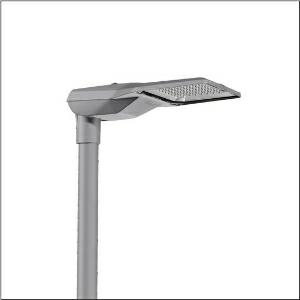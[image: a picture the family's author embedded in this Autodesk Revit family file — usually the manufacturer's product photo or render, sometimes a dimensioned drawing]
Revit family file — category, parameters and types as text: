
# Revit family: streetlight_sl_21_midi___st0_5a_5xe3b33s08nb_b3d9
name_source: partatom
category: Lighting Fixtures
units: mm (PartAtom-declared; Revit-internal decimal feet)

## family parameters
Cut with Voids When Loaded = No
Host = Face
Light Source = No
Part Type = Normal
Room Calculation Point = No
Round Connector Dimension = Use Diameter
Shared = No

## types (1)
- --- (1 x LED, 22700 lm, 151.2 W, 3000K)
    Apparent Load = 151 VA
    CIE Flux Codes = 43 76 97 100 100
    Color Rendering = 70
    Color Temperature = 3000K
    Default Elevation = 1800 mm
    Description = Streetlight SL 21 midi, mast luminaire, primary light control with lens, of PMMA, primary optical cover: cover, of toughened safety glass, transparent, light distribution: ST0.5a, light emission: direct distribution, primary light characteristic: asymmetric, installation type: side-entry, post-top, LED, High Power LED, rated luminous flux: 22.700lm, luminous efficacy: 150lm/W, light colour: 730, colour temperature: 3000K, control gear: D4i, control: overheat protection, constant luminous flux control, time-dependent luminous flux control, flexible luminous flux parameterisation, pre-setting: logarithmic dimming characteristic, mains connection: 230..240V, AC, 50/60Hz, start of lifetime: 151W, end of service life: 157W, reduction: 70W, luminaire housing, of diecast aluminium, powder-coated, Siteco® metallic grey (DB 702S), corrosivity category C5 mid according to DIN EN ISO 12944, please order mast flange separately, inclination adjustable: 0°, 5°, 10°, 15°, sealing non-destructively replaceable, multi-level sealing system, length: 644mm, width: 335mm, height: 110mm, mast flange for spigot size: 42mm (side-entry): 5XC10008XM4, 60/48mm (side-entry/post-top): 5XC10108XM2, 76/60mm (side-entry/post-top): 5XC10108XM1, mounting height: 4..8m, Smart Interface above, protection rating (complete): IP66, insulation class (complete): insulation class II (safety insulation), certification: CE, ENEC, ENEC+, VDE, impact resistance: IK10, permissible operating ambient temperature for outdoor applications: -40..+50°C, standard-compliant lighting for roads and squares, packaging unit: 1 piece

Light Distribution: ST0.5a
    Height = 111 mm
    Lamp = 1 x LED
    Lamp Light Flux = 22700 lm
    Lamp Power = 151.2 W
    Lamp count = 1
    Length = 644 mm
    Luminous efficacy = 150 lm/W
    Manufacturer = Siteco
    ModVariant = No
    Model = 5XE3B33S08NB
    Number of Poles = 1
    OnlyDefault = Yes
    Power Factor = 1
    Product Name = Streetlight SL 21 midi | ST0.5a
    Product group = mast luminaire | pylon top
    ProductGroupID = 6100
    Protection Class = Protection class II
    Protection Degree = IP 66
    RLX_Detail_Level = 1
    RLX_Emergency_Light_Flux = 0 lm
    RLX_Emergency_Type = 0
    RLX_Emergency_Type_DB = No
    RlxData = <blob elided: 38025 chars, md5=d5f1faeb>
    Socket = socket
    Standby Power = 0 W
    System Light Flux = 22700 lm
    System Power = 151 W
    Type Comments = factory setting: luminous flux: 100 % | dim-lin: 254 | 802 mA
    Type Image = l_1004302.jpg
    URL = http://relux.com
    VarID = @adj_192893
    Voltage = 0 V
    Weight = 0.00 kg
    Width = 336 mm

## geometry (parser evidence)
native form markers: Blend x4, Sweep x10
no freeform markers — native parametric forms only
